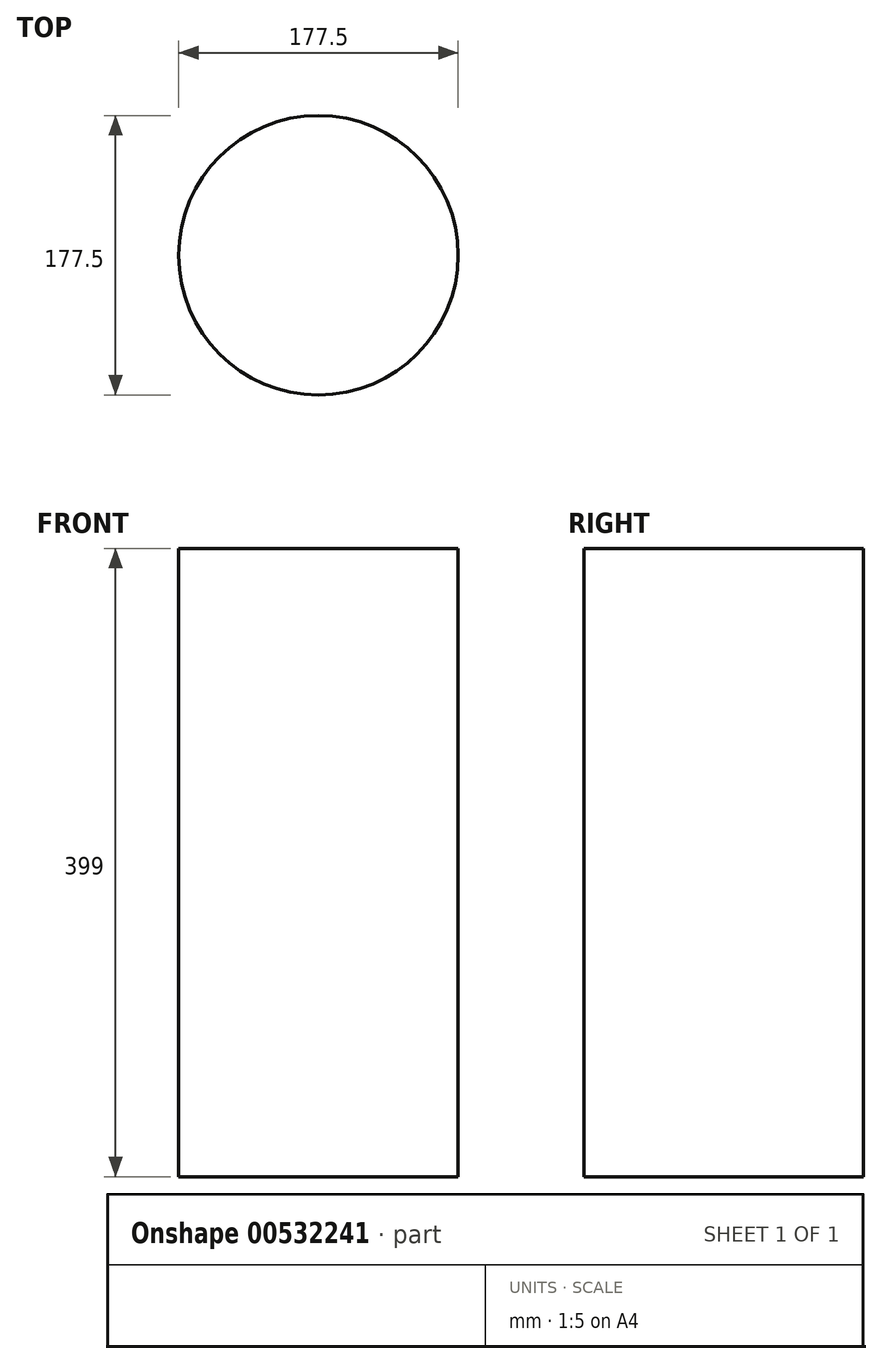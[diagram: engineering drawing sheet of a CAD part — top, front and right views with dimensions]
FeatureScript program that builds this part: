
annotation { "Feature Type Name" : "Feature", "Feature Type Description" : "" }
export const myFeature = defineFeature(function(context is Context, id is Id, definition is map)
    precondition{}
    {
        {
            var Q0;
            Q0=qCreatedBy(makeId("Top.planeOp"),FACE);
            var sketch = newSketch(context, id + "F0", { "sketchPlane" : qUnion([Q0])});
            skCircle(sketch, "E0", {"center": v(0, 0) * mm, "radius": 88.75 * mm});
            skSolve(sketch);
        }
        {
            var Q0;
            Q0 = qSketchRegion(id + "F0", true);
            extrude(context, id + "F1", {"entities" : qUnion([Q0]), "oppositeDirection" : true, "depth" : 399 * mm, "offsetDistance" : 25 * mm});
        }
    });
